# Revit family: Hager-VOLTA-Surface_mounted-IP30-With_Cover-With_DIN-Hosted-CH-de
name_source: partatom
category: Electrical Equipment
units: mm (PartAtom-declared; Revit-internal decimal feet)

## family parameters
Cut with Voids When Loaded = No
Host = Face
Maintain Annotation Orientation = Yes
Panel Configuration = Two Columns, Circuits Across
Part Type = Panelboard
Room Calculation Point = No
Round Connector Dimension = Use Diameter
Shared = No

## types (10) — shared parameters
BC_MODEL_ID = 1547130
BC_OBJECT_ID = 513471
BC_OBJECT_VERSION = #9
Code hager = ADD-EC000214_EU
EF000003 - Montageart = Aufputz
EF000008 - Breite = 305 mm  [stored 1.00066 ft]
EF000024 - UV-beständig = No
EF000049 - Tiefe = 96 mm  [stored 0.314961 ft]
EF000116 - RAL-Nummer = 9010
EF001062 - EMV-Ausführung = No
EF001134 - DIN-Schiene = Yes
EF002950 - Anzahl Teilungseinheiten = 12
EF005474 - Schutzart (IP) = IP30
EF006244 - Transparenter Deckel/Tür = No
EF006306 - Mit Schloss = No
EF015777 - Neutralleiterklemmenblock = No
ETIM class code = EC000214
ETIM class name = Small distribution board
HG000001-Anzahl der Spalten = 1
HG000002-Mit tür = Yes
HG000003-Bereich = VOLTA
HG000005-Dicke = 2 mm  [stored 0.00656168 ft]
HG000006-Unterputz = No
HG000009-Doppelflügeligen Tür = No
HG000010-Asymmetrische Türen = No
HG000012-Türschwenkwinkel = 90.00°
HG000013-Tür links = No
HG000014-Tür rechts = Yes
HG000015-Sichtbarkeit der Türöffnung = Yes
HG000016-3D-Türsichtbarkeit = Yes
HG000017-Distanz zwischen den Polen = 18 mm  [stored 0.0590551 ft]
HG000060-RAL-number = 9010
HG000099-Onfly Template ID-de-CH = 507532
HGEF0002950-Breite in Teilungseinheiten = 12
Manufacturer = Hager
Name = VOLTA-Surface_mounted-IP30-With_Cover-With_DIN-CH
Name BIM&CO = Electricity
Name hager = ADD_Enclosures_EC000214
Uniformat = Low Tension Service & Dist.
Uniformat code = D501001
zero-valued in all types: Default Elevation, EF000218 - Einbautiefe, EF000846 - Einbaubreite, EF001131 - Innentiefe, HG000007-Anzahl der leeren Spalten

## per-type parameters (varying)
| type | BC_VARIANT_ID | EF000007 - Farbe | EF000040 - Höhe | EF000118 - Mit Montageplatte | EF000266 - Anzahl der Reihen | EF000332 - Einbauhöhe | EF001088 - Anbaumöglichkeit | EF004462 - Art der Schliessung | EF009212 - Ausführung Deckel | EF015776 - Erdungsklemmenblock | EF015941 - Signaldurchlassende Tür | HG000004-Herstellerreferenz | HG000008-Anzahl der leeren Reihen | HG000011-Leere Reihen von unten | HGEF000266-Anzahl der Reihen |
| VOLTA-Surface_mounted_W305_H245_D96_12_Modular_Spacing-VA12A | 1174202 |  | 245 mm  [stored 0.803806 ft] | No | 1 | 0 mm  [stored 0 ft] | No |  |  | No | No | VA12A | 0 | No | 1 |
| VOLTA-Surface_mounted_W305_H370_D96_12_Modular_Spacing-VA24A | 1174203 | weiss | 370 mm  [stored 1.21391 ft] | No | 2 | 0 mm  [stored 0 ft] | Yes | sonstige | mit Ausschnitt | Yes | No | VA24A | 0 | No | 2 |
| VOLTA-Surface_mounted_W305_H515_D96_12_Modular_Spacing-VA36A | 1174204 | weiss | 515 mm  [stored 1.68963 ft] | No | 3 | 0 mm  [stored 0 ft] | Yes | sonstige | mit Ausschnitt | Yes | No | VA36A | 0 | No | 3 |
| VOLTA-Surface_mounted_W305_H515_D96_12_Modular_Spacing-VA36RM | 1174207 | weiss | 515 mm  [stored 1.68963 ft] | No | 3 | 0 mm  [stored 0 ft] | Yes | sonstige | mit Ausschnitt | No | No | VA36RM | 0 | No | 3 |
| VOLTA-Surface_mounted_W305_H640_D96_12_Modular_Spacing-VA48A | 1174211 | weiss | 640 mm  [stored 2.09974 ft] | No | 4 | 0 mm  [stored 0 ft] | Yes | sonstige | mit Ausschnitt | Yes | No | VA48A | 0 | No | 4 |
| VOLTA-Surface_mounted_W305_H765_D96_12_Modular_Spacing-VA602NWS | 1174212 | weiss | 765 mm  [stored 2.50984 ft] | Yes | 5 | 765 mm  [stored 2.50984 ft] | Yes | sonstige | mit Ausschnitt | Yes | No | VA602NWS | 3 | Yes | 5 |
| VOLTA-Surface_mounted_W305_H765_D96_12_Modular_Spacing-VA602WWS | 1174213 | weiss | 765 mm  [stored 2.50984 ft] | Yes | 5 | 765 mm  [stored 2.50984 ft] | Yes | sonstige | mit Ausschnitt | Yes | Yes | VA602WWS | 3 | Yes | 5 |
| VOLTA-Surface_mounted_W305_H765_D96_12_Modular_Spacing-VA603NWS | 1174214 | weiss | 765 mm  [stored 2.50984 ft] | Yes | 5 | 765 mm  [stored 2.50984 ft] | Yes | sonstige | mit Ausschnitt | Yes | No | VA603NWS | 2 | Yes | 5 |
| VOLTA-Surface_mounted_W305_H765_D96_12_Modular_Spacing-VA603WWS | 1174215 | weiss | 765 mm  [stored 2.50984 ft] | Yes | 5 | 765 mm  [stored 2.50984 ft] | Yes | sonstige | mit Ausschnitt | Yes | Yes | VA603WWS | 2 | Yes | 5 |
| VOLTA-Surface_mounted_W305_H765_D96_12_Modular_Spacing-VA60A | 1174216 | weiss | 765 mm  [stored 2.50984 ft] | No | 5 | 0 mm  [stored 0 ft] | Yes | sonstige | mit Ausschnitt | Yes | No | VA60A | 0 | No | 5 |

note: column(s) folded — value = type name in every type: Reference

note: [stored X ft] marks values corroborated as IEEE doubles in the binary element streams (Revit-internal decimal feet)

## geometry (parser evidence)
native form markers: Sweep x15
no freeform markers — native parametric forms only
